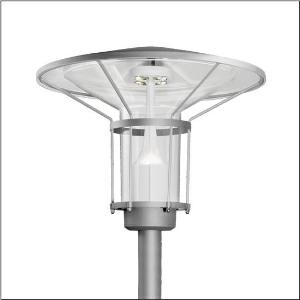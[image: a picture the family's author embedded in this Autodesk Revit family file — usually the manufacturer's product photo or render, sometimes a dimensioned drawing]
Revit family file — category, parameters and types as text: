
# Revit family: laterne_classic_iq___p1_0a_5xa5245lf14h_4a87
name_source: partatom
category: Lighting Fixtures
units: mm (PartAtom-declared; Revit-internal decimal feet)

## family parameters
Cut with Voids When Loaded = No
Host = Face
Light Source = No
Part Type = Normal
Room Calculation Point = No
Round Connector Dimension = Use Diameter
Shared = No

## types (1)
- --- (1 x LED, 1360 lm, 10 W, 4000K)
    Apparent Load = 10 VA
    CIE Flux Codes = 30 61 91 96 100
    Color Rendering = 70
    Color Temperature = 4000K
    Default Elevation = 1800 mm
    Description = Lantern Classic iQ, mast luminaire, Module 540 iQ-SR, primary light control with 3 zone facetted reflector, of plastic, silver coated, highly specular, structured, primary optical cover: cover, of PMMA, transparent, light distribution: P1.0a, light emission: direct distribution, primary light characteristic: strongly asymmetric, installation type: post-top, LED, High Power LED, rated luminous flux: 1.360lm, luminous efficacy: 136lm/W, light colour: 740, colour temperature: 4000K, control gear: ECG iQ, control: presetting dimming logarithmic, Street-Remote, Auto-Match, Temp-Guard, Lumen-Switch, Night-Set, Smart-Wire, Light-Fading, Desk-Remote (wireless, voltage-free reading and setting of iQ features in the workshop via application-optimized NFC function/RFID function), optimised constant luminous flux control (CLO 2.0), with terminal, 6-pole, max. 2.5mm², mains connection: 230..240V, AC, 50/60Hz, start of lifetime: 10W, end of service life: 10W, reduction: 5W, luminaire housing, upper part, of glass-fibre reinforced polyester, coated, Siteco® metallic grey (DB 702S), diameter: 750mm, height: 596mm, spigot size: d x l = 76 x 70mm (post-top) | with reducer (optional accessory) 60 x 70mm, post-top mast mounting element, of diecast aluminium, coated, Siteco® metallic grey (DB 702S), Module 540 iQ-SR, traffic white (RAL 9016), equipment: standard, protection rating (complete): IP65, insulation class (complete): insulation class II (safety insulation), certification: CE, ENEC, VDE, packaging unit: 1 piece

Light Distribution: P1.0a
    Height = 596 mm
    Lamp = 1 x LED
    Lamp Light Flux = 1360 lm
    Lamp Power = 10 W
    Lamp count = 1
    Length = 750 mm
    Luminous efficacy = 136 lm/W
    Manufacturer = Siteco
    ModVariant = No
    Model = 5XA5245LF14H
    Number of Poles = 1
    OnlyDefault = Yes
    Power Factor = 1
    Product Name = Laterne Classic iQ | P1.0a
    Product group = mast luminaire | pylon top
    ProductGroupID = 6100
    Protection Class = Protection class II
    Protection Degree = IP 65
    RLX_Detail_Level = 1
    RLX_Emergency_Light_Flux = 0 lm
    RLX_Emergency_Type = 0
    RLX_Emergency_Type_DB = No
    RlxData = <blob elided: 98361 chars, md5=6ac661a7>
    Socket = socket
    Standby Power = 0 W
    System Light Flux = 1360 lm
    System Power = 10 W
    Type Comments = factory setting: luminous flux: 100 % | dim-lin: 254 | 401 mA
    Type Image = l_1006052.jpg
    URL = http://relux.com
    VarID = @adj_110389
    Voltage = 0 V
    Weight = 0.00 kg
    Width = 0 mm  [stored 0 ft]

note: [stored X ft] marks values corroborated as IEEE doubles in the binary element streams (Revit-internal decimal feet)

## geometry (parser evidence)
native form markers: Blend x4, Sweep x8
no freeform markers — native parametric forms only
